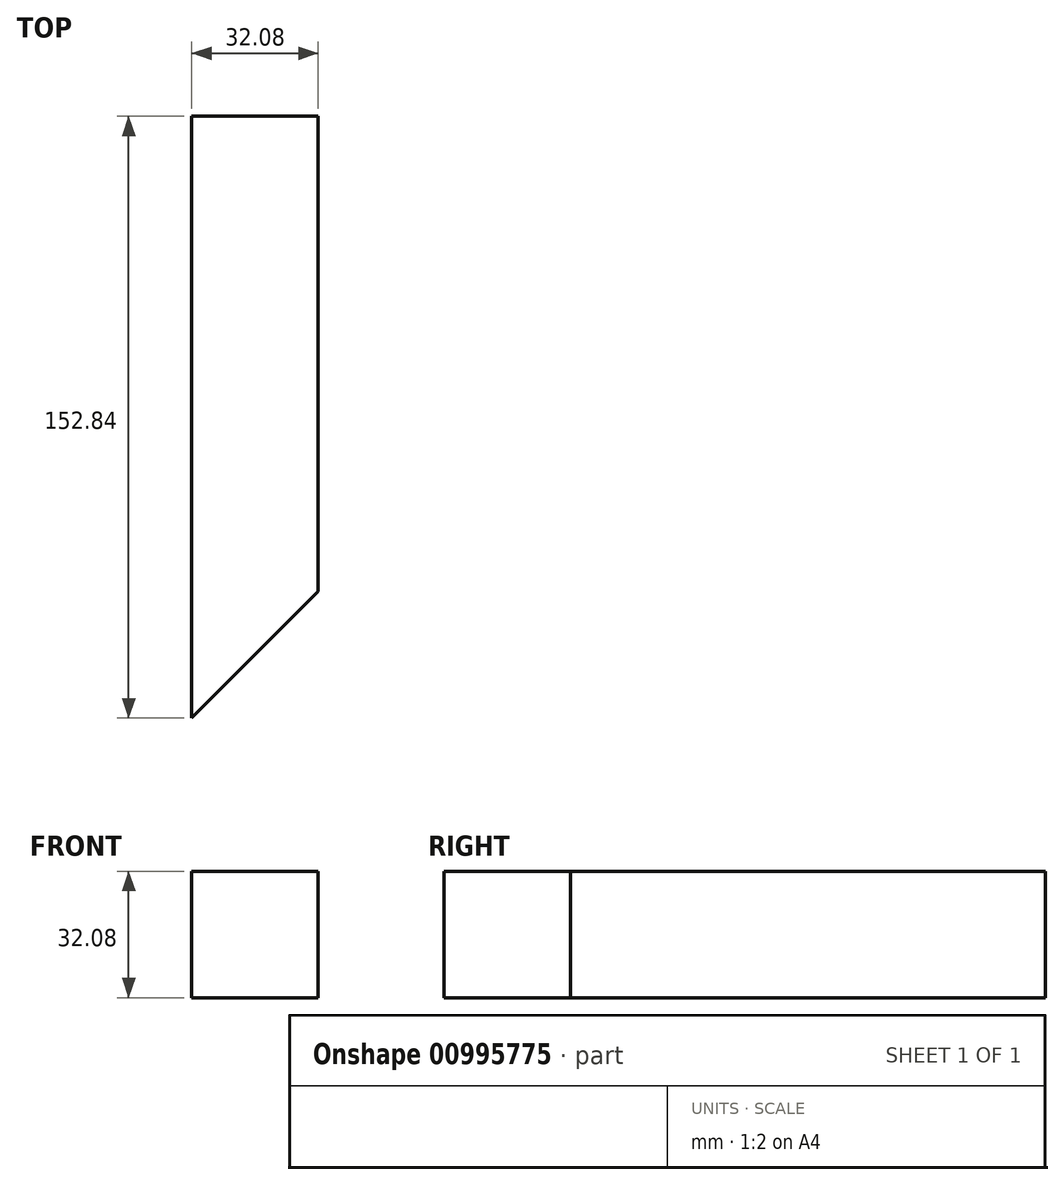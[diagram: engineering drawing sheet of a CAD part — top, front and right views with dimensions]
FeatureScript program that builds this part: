
annotation { "Feature Type Name" : "Feature", "Feature Type Description" : "" }
export const myFeature = defineFeature(function(context is Context, id is Id, definition is map)
    precondition{}
    {
        {
            var Q0;
            Q0=qCreatedBy(makeId("Top.planeOp"),FACE);
            var sketch = newSketch(context, id + "F0", { "sketchPlane" : qUnion([Q0])});
            skLineSegment(sketch, "E0.bottom", {"start": v(16.04, 76.42) * mm, "end": v(-16.04, 76.42) * mm});
            skLineSegment(sketch, "E0.top", {"start": v(16.04, -76.42) * mm, "end": v(-16.04, -76.42) * mm});
            skLineSegment(sketch, "E0.left", {"start": v(16.04, 76.42) * mm, "end": v(16.04, -76.42) * mm});
            skLineSegment(sketch, "E0.right", {"start": v(-16.04, 76.42) * mm, "end": v(-16.04, -76.42) * mm});
            skPoint(sketch, "E0.middle", {"position": v(0, 0) * mm});
            skSolve(sketch);
        }
        {
            var Q0;
            Q0=makeQuery(id+"F0.imprint","IMPRINT",FACE,{"disambiguationData":[TD([[makeQuery(id+"F0.imprint","IMPRINT",EDGE,{"derivedFrom":sQuery(id+"F0.wireOp",EDGE,"E0.bottom")}),1.0]])]});
            extrude(context, id + "F1", {"entities" : qUnion([Q0]), "endBound" : BoundingType.SYMMETRIC, "depth" : 32.08 * mm, "offsetDistance" : 25.4 * mm});
        }
        {
            var Q0;
            Q0=makeQuery(id+"F1.opExtrude","CAP_FACE",FACE,{"disambiguationData":[OSD([sQuery(id+"F0.wireOp",EDGE,"E0.bottom"),sQuery(id+"F0.wireOp",EDGE,"E0.top"),sQuery(id+"F0.wireOp",EDGE,"E0.left"),sQuery(id+"F0.wireOp",EDGE,"E0.right")])],"isStart":false});
            var sketch = newSketch(context, id + "F2", { "sketchPlane" : qUnion([Q0])});
            skLineSegment(sketch, "E1", {"start": v(16.04, -76.42) * mm, "end": v(16.04, -44.34) * mm});
            skLineSegment(sketch, "E2", {"start": v(16.04, -44.34) * mm, "end": v(-16.04, -76.42) * mm});
            skLineSegment(sketch, "E3", {"start": v(-16.04, -76.42) * mm, "end": v(16.04, -76.42) * mm});
            skSolve(sketch);
        }
        {
            var Q0;
            Q0=qSketchRegion(id+"F2",true);
            extrude(context, id + "F3", {"entities" : qUnion([Q0]), "operationType" : NewBodyOperationType.REMOVE, "endBound" : BoundingType.UP_TO_NEXT, "oppositeDirection" : true, "depth" : 25.4 * mm, "offsetDistance" : 25.4 * mm});
        }
    });
